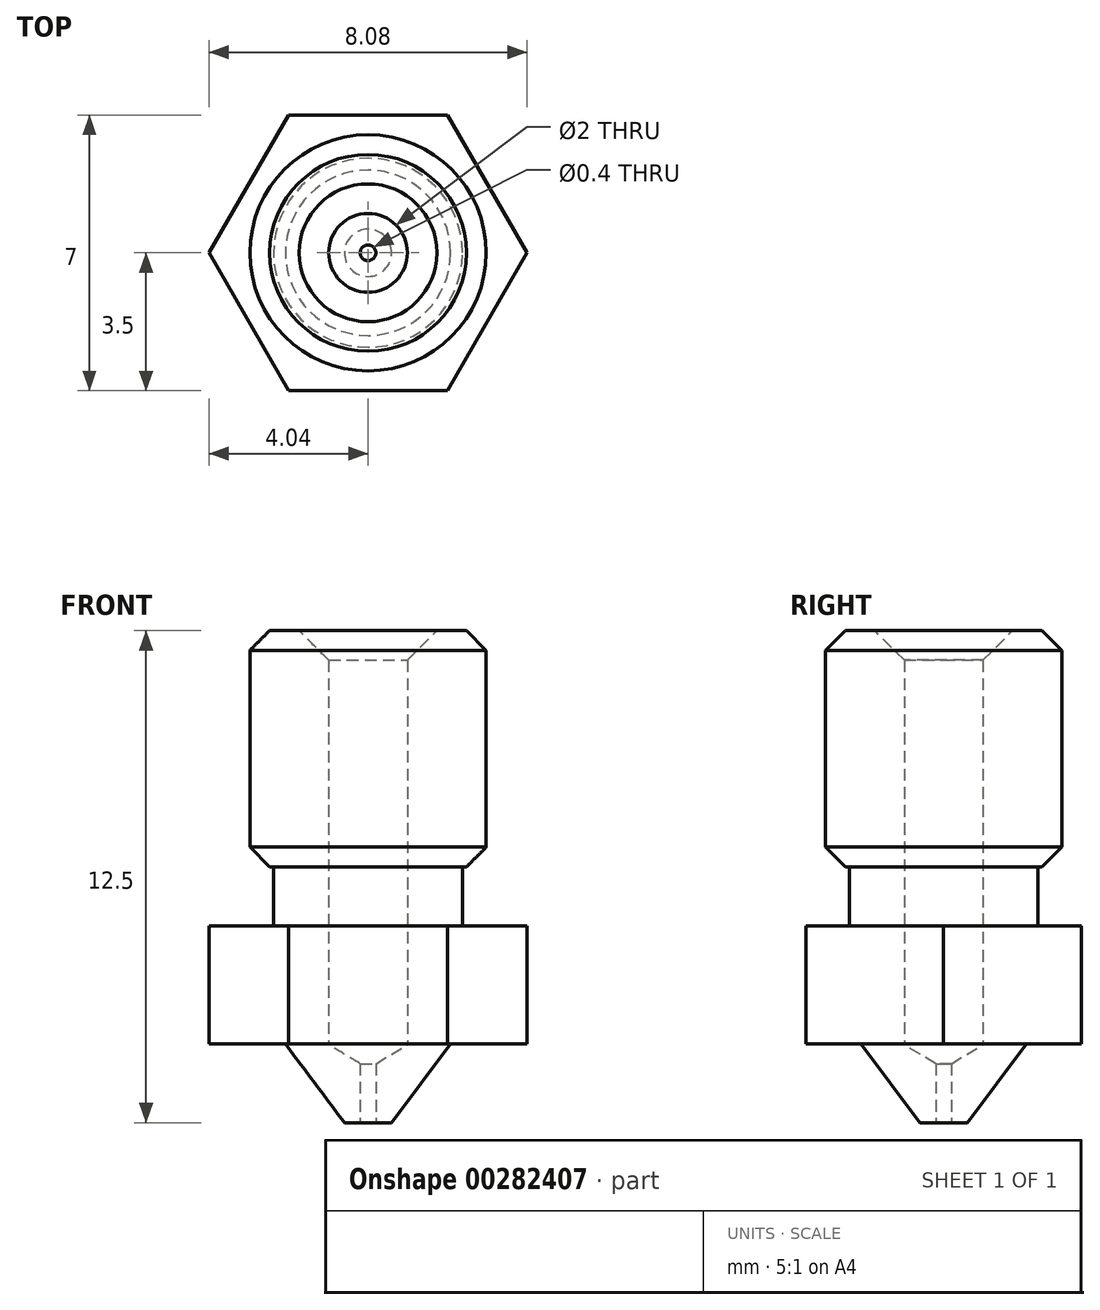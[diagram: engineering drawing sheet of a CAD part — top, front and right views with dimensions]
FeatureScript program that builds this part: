
annotation { "Feature Type Name" : "Feature", "Feature Type Description" : "" }
export const myFeature = defineFeature(function(context is Context, id is Id, definition is map)
    precondition{}
    {
        {
            var Q0;
            Q0=qCreatedBy(makeId("Front.planeOp"),FACE);
            var sketch = newSketch(context, id + "F0", { "sketchPlane" : qUnion([Q0])});
            skLineSegment(sketch, "E0", {"start": v(0, 0) * mm, "end": v(0, 12.5) * mm, "construction": true});
            skLineSegment(sketch, "E1", {"start": v(0.2, 0) * mm, "end": v(0.2, 1.5) * mm});
            skLineSegment(sketch, "E2", {"start": v(0.2, 0) * mm, "end": v(0.6, 0) * mm});
            skLineSegment(sketch, "E3", {"start": v(0.6, 0) * mm, "end": v(2.1, 2) * mm});
            skLineSegment(sketch, "E4", {"start": v(2.1, 2) * mm, "end": v(4.2, 2) * mm});
            skLineSegment(sketch, "E5", {"start": v(4.2, 2) * mm, "end": v(4.2, 5) * mm});
            skLineSegment(sketch, "E6", {"start": v(1, 12.5) * mm, "end": v(1, 1.98) * mm});
            skLineSegment(sketch, "E7", {"start": v(1, 1.98) * mm, "end": v(0.2, 1.5) * mm});
            skLineSegment(sketch, "E8", {"start": v(1, 12.5) * mm, "end": v(3, 12.5) * mm});
            skLineSegment(sketch, "E9", {"start": v(3, 12.5) * mm, "end": v(3, 6.5) * mm});
            skLineSegment(sketch, "E10", {"start": v(3, 6.5) * mm, "end": v(2.4, 6.5) * mm});
            skLineSegment(sketch, "E11", {"start": v(2.4, 6.5) * mm, "end": v(2.4, 5) * mm});
            skLineSegment(sketch, "E12", {"start": v(2.4, 5) * mm, "end": v(4.2, 5) * mm});
            skSolve(sketch);
        }
        {
            var Q0;
            Q0=qSketchRegion(id+"F0",true);
            var Q1;
            Q1=sQuery(id+"F0.wireOp",EDGE,"E0");
            revolve(context, id + "F1", {"entities" : qUnion([Q0]), "axis" : qUnion([Q1]), "revolveType" : RevolveType.FULL});
        }
        {
            var Q0;
            Q0=makeQuery(id+"F1.opRevolve","SWEPT_EDGE",EDGE,{"disambiguationData":[OSD([sQuery(id+"F0.wireOp",EDGE,"E9"),sQuery(id+"F0.wireOp",EDGE,"E10")])]});
            var Q1;
            Q1=makeQuery(id+"F1.opRevolve","SWEPT_EDGE",EDGE,{"disambiguationData":[OSD([sQuery(id+"F0.wireOp",EDGE,"E8"),sQuery(id+"F0.wireOp",EDGE,"E9")])]});
            chamfer(context, id + "F2", {"entities" : qUnion([Q0, Q1]), "width" : 0.5 * mm, "tangentPropagation" : true});
        }
        {
            var Q0;
            Q0=makeQuery(id+"F1.opRevolve","SWEPT_EDGE",EDGE,{"disambiguationData":[OSD([sQuery(id+"F0.wireOp",EDGE,"E6"),sQuery(id+"F0.wireOp",EDGE,"E8")])]});
            chamfer(context, id + "F3", {"entities" : qUnion([Q0]), "width" : 0.75 * mm, "tangentPropagation" : true});
        }
        {
            var Q0;
            Q0=makeQuery(id+"F1.opRevolve","SWEPT_FACE",FACE,{"disambiguationData":[OSD([sQuery(id+"F0.wireOp",EDGE,"E4")])]});
            var sketch = newSketch(context, id + "F4", { "sketchPlane" : qUnion([Q0])});
            skCircle(sketch, "E13.cCircle", {"center": v(0, 0) * mm, "radius": 3.5 * mm, "construction": true});
            skLineSegment(sketch, "E13.0", {"start": v(-2.02, -3.5) * mm, "end": v(-4.04, 0) * mm});
            skLineSegment(sketch, "E13.1", {"start": v(-4.04, 0) * mm, "end": v(-2.02, 3.5) * mm});
            skLineSegment(sketch, "E13.2", {"start": v(-2.02, 3.5) * mm, "end": v(2.02, 3.5) * mm});
            skLineSegment(sketch, "E13.3", {"start": v(2.02, 3.5) * mm, "end": v(4.04, 0) * mm});
            skLineSegment(sketch, "E13.4", {"start": v(4.04, 0) * mm, "end": v(2.02, -3.5) * mm});
            skLineSegment(sketch, "E13.5", {"start": v(2.02, -3.5) * mm, "end": v(-2.02, -3.5) * mm});
            skPoint(sketch, "E13.0.midPoint", {"position": v(-3.03, -1.75) * mm});
            skLineSegment(sketch, "E14", {"start": v(-4.04, 0) * mm, "end": v(0, 0) * mm, "construction": true});
            skCircle(sketch, "E15", {"center": v(0, 0) * mm, "radius": 5 * mm});
            skSolve(sketch);
        }
        {
            var Q0;
            Q0=qSketchRegion(id+"F4",true);
            extrude(context, id + "F5", {"entities" : qUnion([Q0]), "operationType" : NewBodyOperationType.REMOVE, "endBound" : BoundingType.THROUGH_ALL, "oppositeDirection" : true, "depth" : 25 * mm});
        }
    });
